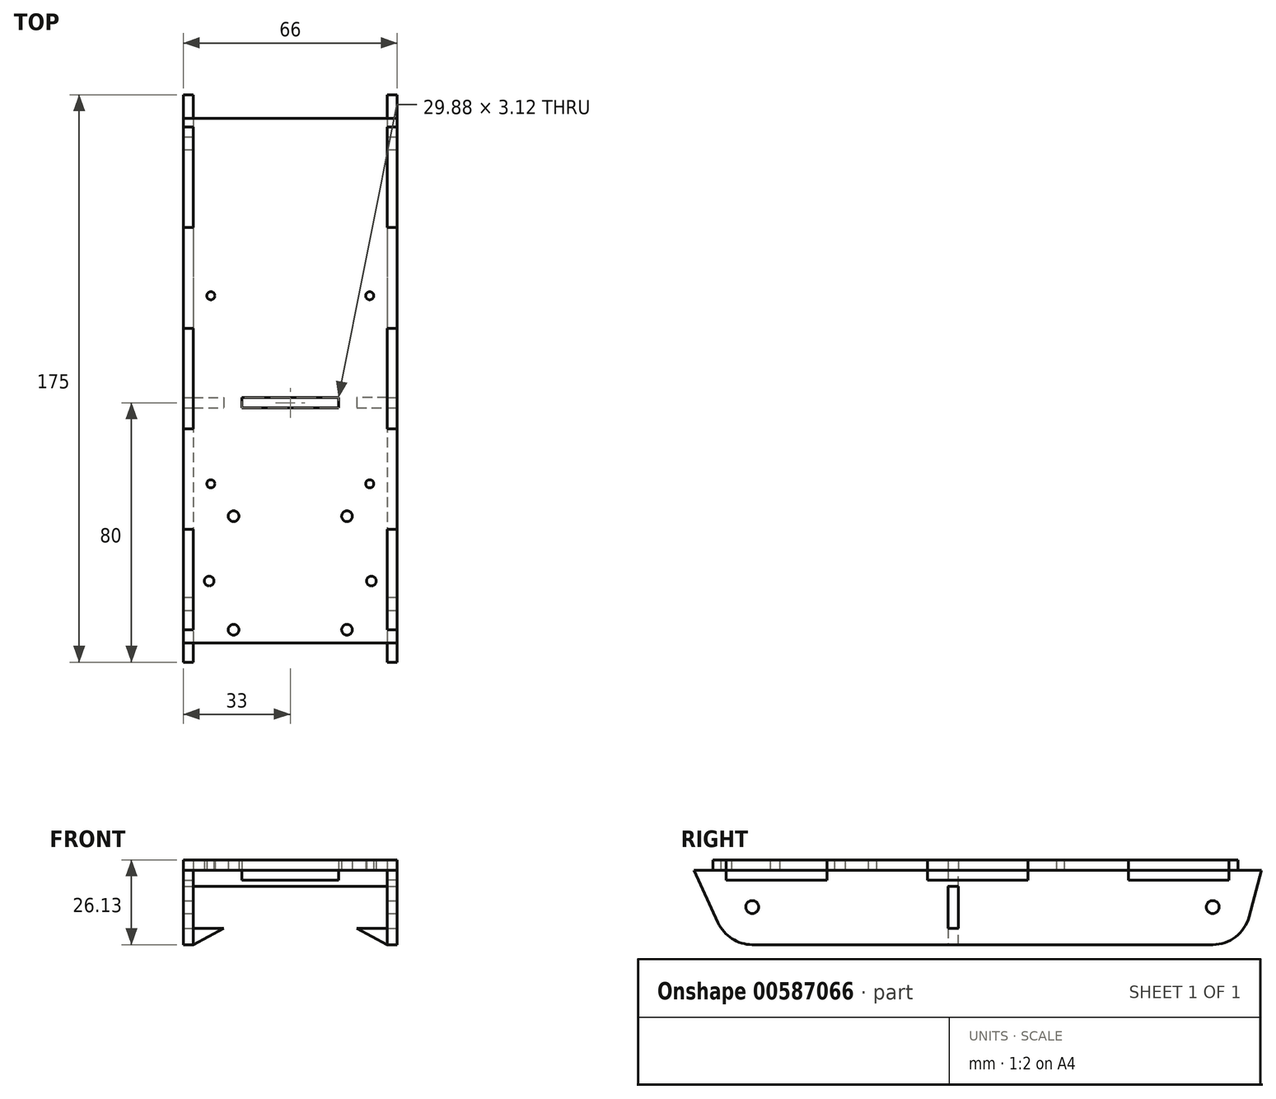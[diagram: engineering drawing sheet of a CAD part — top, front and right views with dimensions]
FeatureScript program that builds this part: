
annotation { "Feature Type Name" : "Feature", "Feature Type Description" : "" }
export const myFeature = defineFeature(function(context is Context, id is Id, definition is map)
    precondition{}
    {
        {
            var Q0;
            Q0=qCreatedBy(makeId("Top.planeOp"),FACE);
            var sketch = newSketch(context, id + "F0", { "sketchPlane" : qUnion([Q0])});
            skLineSegment(sketch, "E0.bottom", {"start": v(-33, 87.5) * mm, "end": v(33, 87.5) * mm});
            skLineSegment(sketch, "E0.top", {"start": v(-33, -87.5) * mm, "end": v(33, -87.5) * mm});
            skLineSegment(sketch, "E0.left", {"start": v(-33, 87.5) * mm, "end": v(-33, -87.5) * mm});
            skLineSegment(sketch, "E0.right", {"start": v(33, 87.5) * mm, "end": v(33, -87.5) * mm});
            skLineSegment(sketch, "E1", {"start": v(0, 87.5) * mm, "end": v(0, -87.5) * mm, "construction": true});
            skLineSegment(sketch, "E2", {"start": v(-33, 0) * mm, "end": v(33, 0) * mm, "construction": true});
            skCircle(sketch, "E3", {"center": v(-25, -62.5) * mm, "radius": 1.5 * mm});
            skCircle(sketch, "E4.MirrorC", {"center": v(25, -62.5) * mm, "radius": 1.5 * mm});
            skLineSegment(sketch, "E5", {"start": v(-50, -69.5) * mm, "end": v(50, -69.5) * mm, "construction": true});
            skLineSegment(sketch, "E6", {"start": v(-33.17, -7.5) * mm, "end": v(44.72, -7.5) * mm, "construction": true});
            skCircle(sketch, "E7", {"center": v(-24.5, 25.5) * mm, "radius": 1.25 * mm});
            skCircle(sketch, "E8", {"center": v(-24.5, -32.5) * mm, "radius": 1.25 * mm});
            skCircle(sketch, "E9.MirrorC", {"center": v(24.5, -32.5) * mm, "radius": 1.25 * mm});
            skCircle(sketch, "E10.MirrorC", {"center": v(24.5, 25.5) * mm, "radius": 1.25 * mm});
            skCircle(sketch, "E11", {"center": v(-17.5, -42.5) * mm, "radius": 1.65 * mm});
            skCircle(sketch, "E12", {"center": v(-17.5, -77.5) * mm, "radius": 1.65 * mm});
            skCircle(sketch, "E13.MirrorC", {"center": v(17.5, -77.5) * mm, "radius": 1.65 * mm});
            skCircle(sketch, "E14.MirrorC", {"center": v(17.5, -42.5) * mm, "radius": 1.65 * mm});
            skSolve(sketch);
        }
        {
            var Q0;
            Q0 = qSketchRegion(id + "F0", true);
            extrude(context, id + "F1", {"entities" : qUnion([Q0]), "depth" : 3.12 * mm, "offsetDistance" : 25 * mm});
        }
        {
            var Q0;
            Q0=qCreatedBy(makeId("Top.planeOp"),FACE);
            var sketch = newSketch(context, id + "F2", { "sketchPlane" : qUnion([Q0])});
            skLineSegment(sketch, "E15.bottom", {"start": v(-33, 87.5) * mm, "end": v(-29.88, 87.5) * mm});
            skLineSegment(sketch, "E15.top", {"start": v(-33, -87.5) * mm, "end": v(-29.87, -87.5) * mm});
            skLineSegment(sketch, "E15.left", {"start": v(-33, 87.5) * mm, "end": v(-33, -87.5) * mm});
            skLineSegment(sketch, "E15.right", {"start": v(-29.88, 87.5) * mm, "end": v(-29.87, -87.5) * mm});
            skLineSegment(sketch, "E16.MirrorCS", {"start": v(33, 87.5) * mm, "end": v(29.88, 87.5) * mm});
            skLineSegment(sketch, "E17.MirrorCS", {"start": v(33, -87.5) * mm, "end": v(29.87, -87.5) * mm});
            skLineSegment(sketch, "E18.MirrorCS", {"start": v(29.88, 87.5) * mm, "end": v(29.87, -87.5) * mm});
            skLineSegment(sketch, "E19.MirrorCS", {"start": v(33, 87.5) * mm, "end": v(33, -87.5) * mm});
            skSolve(sketch);
        }
        {
            var Q0;
            Q0 = qSketchRegion(id + "F2", true);
            extrude(context, id + "F3", {"entities" : qUnion([Q0]), "oppositeDirection" : true, "depth" : 23 * mm, "offsetDistance" : 25 * mm});
        }
        {
            var Q0;
            Q0=qCreatedBy(makeId("Right.planeOp"),FACE);
            var sketch = newSketch(context, id + "F4", { "sketchPlane" : qUnion([Q0])});
            skCircle(sketch, "E20", {"center": v(-69.5, -11.4) * mm, "radius": 2 * mm});
            skCircle(sketch, "E21", {"center": v(72.5, -11.4) * mm, "radius": 2 * mm});
            skLineSegment(sketch, "E22", {"start": v(80.27, 0) * mm, "end": v(80.27, 7.65) * mm});
            skLineSegment(sketch, "E23", {"start": v(80.27, 7.65) * mm, "end": v(-81.6, 7.65) * mm});
            skLineSegment(sketch, "E24", {"start": v(-81.6, 7.65) * mm, "end": v(-81.6, 0) * mm});
            skLineSegment(sketch, "E25", {"start": v(-87.5, 0) * mm, "end": v(-81.6, 0) * mm});
            skLineSegment(sketch, "E26", {"start": v(-87.5, 0) * mm, "end": v(-80.04, -16.24) * mm});
            skLineSegment(sketch, "E27", {"start": v(87.5, 0) * mm, "end": v(80.27, 0) * mm});
            skLineSegment(sketch, "E28", {"start": v(87.5, 0) * mm, "end": v(83.72, -14.36) * mm});
            skArc(sketch, "E29", {"start": v(83.72, -14.36) * mm, "mid": v(79.58, -20.59) * mm, "end": v(72.5, -23) * mm});
            skArc(sketch, "E30", {"start": v(-80.04, -16.24) * mm, "mid": v(-75.76, -21.17) * mm, "end": v(-69.5, -23) * mm});
            skLineSegment(sketch, "E31", {"start": v(72.5, -23) * mm, "end": v(-69.5, -23) * mm});
            skSolve(sketch);
        }
        {
            var Q0;
            Q0 = qSketchRegion(id + "F4", true);
            extrude(context, id + "F5", {"entities" : qUnion([Q0]), "operationType" : NewBodyOperationType.INTERSECT, "endBound" : BoundingType.THROUGH_ALL, "oppositeDirection" : true, "depth" : 25 * mm, "offsetDistance" : 25 * mm, "hasSecondDirection" : true, "secondDirectionBound" : BoundingType.THROUGH_ALL, "secondDirectionOppositeDirection" : false, "secondDirectionDepth" : 25 * mm});
        }
        {
            var Q0;
            Q0=qCreatedBy(makeId("Front.planeOp"),FACE);
            var sketch = newSketch(context, id + "F6", { "sketchPlane" : qUnion([Q0])});
            skLineSegment(sketch, "E32", {"start": v(0, 0) * mm, "end": v(-29.88, 0) * mm});
            skLineSegment(sketch, "E33", {"start": v(-29.88, 0) * mm, "end": v(-29.88, -23) * mm});
            skLineSegment(sketch, "E34", {"start": v(-29.88, -23) * mm, "end": v(-14.88, -15) * mm});
            skLineSegment(sketch, "E35", {"start": v(-14.88, -15) * mm, "end": v(0, -15) * mm});
            skLineSegment(sketch, "E36", {"start": v(0, 0) * mm, "end": v(0, -15) * mm, "construction": true});
            skLineSegment(sketch, "E37.MirrorCS", {"start": v(29.88, -23) * mm, "end": v(14.87, -15) * mm});
            skLineSegment(sketch, "E38.MirrorCS", {"start": v(14.88, -15) * mm, "end": v(0, -15) * mm});
            skLineSegment(sketch, "E39.MirrorCS", {"start": v(29.88, 0) * mm, "end": v(29.88, -23) * mm});
            skLineSegment(sketch, "E40.MirrorCS", {"start": v(0, 0) * mm, "end": v(29.88, 0) * mm});
            skSolve(sketch);
        }
        {
            var Q0;
            Q0 = qSketchRegion(id + "F6", true);
            var Q1;
            Q1=sQuery(id+"F0.wireOp",VERTEX,"E6.start");
            var Q2;
            Q2=sQuery(id+"F0.wireOp",VERTEX,"E6.end");
            extrude(context, id + "F7", {"entities" : qUnion([Q0]), "endBound" : BoundingType.UP_TO_VERTEX, "depth" : 3.12 * mm, "endBoundEntityVertex" : qUnion([Q1]), "hasOffset" : true, "offsetDistance" : (3.12 / 2) * mm, "offsetOppositeDirection" : true, "hasSecondDirection" : true, "secondDirectionBound" : BoundingType.UP_TO_VERTEX, "secondDirectionOppositeDirection" : false, "secondDirectionDepth" : (3.12 / 2) * mm, "secondDirectionBoundEntityVertex" : qUnion([Q2]), "hasSecondDirectionOffset" : true, "secondDirectionOffsetDistance" : (3.12 / 2) * mm});
        }
        {
            var Q0;
            Q0=qCreatedBy(makeId("Right.planeOp"),FACE);
            var sketch = newSketch(context, id + "F8", { "sketchPlane" : qUnion([Q0])});
            skLineSegment(sketch, "E41.bottom", {"start": v(-5.94, -18) * mm, "end": v(-9.06, -18) * mm});
            skLineSegment(sketch, "E41.top", {"start": v(-5.94, -5) * mm, "end": v(-9.06, -5) * mm});
            skLineSegment(sketch, "E41.left", {"start": v(-9.06, -18) * mm, "end": v(-9.06, -5) * mm});
            skLineSegment(sketch, "E41.right", {"start": v(-5.94, -18) * mm, "end": v(-5.94, -5) * mm});
            skLineSegment(sketch, "E42", {"start": v(-7.5, 0) * mm, "end": v(-7.5, -18) * mm, "construction": true});
            skSolve(sketch);
        }
        {
            var Q0;
            Q0 = qSketchRegion(id + "F8", true);
            var Q1;
            Q1=makeQuery(id+"F3.opExtrude","SWEPT_FACE",FACE,{"disambiguationData":[OSD([sQuery(id+"F2.wireOp",EDGE,"E19.MirrorCS")])]});
            var Q2;
            Q2=makeQuery(id+"F3.opExtrude","SWEPT_FACE",FACE,{"disambiguationData":[OSD([sQuery(id+"F2.wireOp",EDGE,"E15.left")])]});
            extrude(context, id + "F9", {"entities" : qUnion([Q0]), "operationType" : NewBodyOperationType.ADD, "endBound" : BoundingType.UP_TO_SURFACE, "depth" : 25 * mm, "endBoundEntityFace" : qUnion([Q1]), "offsetDistance" : 25 * mm, "hasSecondDirection" : true, "secondDirectionBound" : BoundingType.UP_TO_SURFACE, "secondDirectionOppositeDirection" : true, "secondDirectionDepth" : 25 * mm, "secondDirectionBoundEntityFace" : qUnion([Q2])});
        }
        {
            var Q0;
            Q0 = qSketchRegion(id + "F8", true);
            extrude(context, id + "F10", {"entities" : qUnion([Q0]), "operationType" : NewBodyOperationType.REMOVE, "endBound" : BoundingType.THROUGH_ALL, "oppositeDirection" : true, "depth" : 25 * mm, "offsetDistance" : 25 * mm, "hasSecondDirection" : true, "secondDirectionBound" : BoundingType.THROUGH_ALL, "secondDirectionOppositeDirection" : false, "secondDirectionDepth" : 25 * mm});
        }
        {
            var Q0;
            Q0=qCreatedBy(makeId("Top.planeOp"),FACE);
            var sketch = newSketch(context, id + "F11", { "sketchPlane" : qUnion([Q0])});
            skLineSegment(sketch, "E43.bottom", {"start": v(-33, 77.5) * mm, "end": v(-29.87, 77.5) * mm});
            skLineSegment(sketch, "E43.top", {"start": v(-33, 46.5) * mm, "end": v(-29.87, 46.5) * mm});
            skLineSegment(sketch, "E43.left", {"start": v(-33, 77.5) * mm, "end": v(-33, 46.5) * mm});
            skLineSegment(sketch, "E43.right", {"start": v(-29.88, 77.5) * mm, "end": v(-29.88, 46.5) * mm});
            skLineSegment(sketch, "E44.bottom", {"start": v(-33, 15.5) * mm, "end": v(-29.87, 15.5) * mm});
            skLineSegment(sketch, "E44.top", {"start": v(-33, -15.5) * mm, "end": v(-29.88, -15.5) * mm});
            skLineSegment(sketch, "E44.left", {"start": v(-33, 15.5) * mm, "end": v(-33, -15.5) * mm});
            skLineSegment(sketch, "E44.right", {"start": v(-29.88, 15.5) * mm, "end": v(-29.88, -15.5) * mm});
            skLineSegment(sketch, "E45.bottom", {"start": v(-14.94, -9.06) * mm, "end": v(0, -9.06) * mm});
            skLineSegment(sketch, "E45.top", {"start": v(-14.94, -5.94) * mm, "end": v(0, -5.94) * mm});
            skLineSegment(sketch, "E45.left", {"start": v(-14.94, -9.06) * mm, "end": v(-14.94, -5.94) * mm});
            skLineSegment(sketch, "E46.bottom", {"start": v(-33, -46.5) * mm, "end": v(-29.87, -46.5) * mm});
            skLineSegment(sketch, "E46.top", {"start": v(-33, -77.5) * mm, "end": v(-29.88, -77.5) * mm});
            skLineSegment(sketch, "E46.left", {"start": v(-33, -46.5) * mm, "end": v(-33, -77.5) * mm});
            skLineSegment(sketch, "E46.right", {"start": v(-29.88, -46.5) * mm, "end": v(-29.88, -77.5) * mm});
            skLineSegment(sketch, "E47", {"start": v(-33, 46.5) * mm, "end": v(-33, 15.5) * mm, "construction": true});
            skLineSegment(sketch, "E48", {"start": v(-33, -15.5) * mm, "end": v(-33, -46.5) * mm, "construction": true});
            skLineSegment(sketch, "E49.MirrorCS", {"start": v(14.94, -9.06) * mm, "end": v(14.94, -5.94) * mm});
            skLineSegment(sketch, "E50.MirrorCS", {"start": v(14.94, -9.06) * mm, "end": v(0, -9.06) * mm});
            skLineSegment(sketch, "E51.MirrorCS", {"start": v(14.94, -5.94) * mm, "end": v(0, -5.94) * mm});
            skLineSegment(sketch, "E52.MirrorCS", {"start": v(33, -77.5) * mm, "end": v(29.88, -77.5) * mm});
            skLineSegment(sketch, "E53.MirrorCS", {"start": v(33, -46.5) * mm, "end": v(29.88, -46.5) * mm});
            skLineSegment(sketch, "E54.MirrorCS", {"start": v(33, -15.5) * mm, "end": v(29.88, -15.5) * mm});
            skLineSegment(sketch, "E55.MirrorCS", {"start": v(33, 15.5) * mm, "end": v(29.87, 15.5) * mm});
            skLineSegment(sketch, "E56.MirrorCS", {"start": v(33, 46.5) * mm, "end": v(29.87, 46.5) * mm});
            skLineSegment(sketch, "E57.MirrorCS", {"start": v(33, 77.5) * mm, "end": v(29.87, 77.5) * mm});
            skLineSegment(sketch, "E58.MirrorCS", {"start": v(29.88, 15.5) * mm, "end": v(29.88, -15.5) * mm});
            skLineSegment(sketch, "E59.MirrorCS", {"start": v(33, 15.5) * mm, "end": v(33, -15.5) * mm});
            skLineSegment(sketch, "E60.MirrorCS", {"start": v(33, -15.5) * mm, "end": v(33, -46.5) * mm, "construction": true});
            skLineSegment(sketch, "E61.MirrorCS", {"start": v(29.88, 77.5) * mm, "end": v(29.88, 46.5) * mm});
            skLineSegment(sketch, "E62.MirrorCS", {"start": v(33, 77.5) * mm, "end": v(33, 46.5) * mm});
            skLineSegment(sketch, "E63.MirrorCS", {"start": v(33, 46.5) * mm, "end": v(33, 15.5) * mm, "construction": true});
            skLineSegment(sketch, "E64.MirrorCS", {"start": v(29.88, -46.5) * mm, "end": v(29.88, -77.5) * mm});
            skLineSegment(sketch, "E65.MirrorCS", {"start": v(33, -46.5) * mm, "end": v(33, -77.5) * mm});
            skLineSegment(sketch, "E66", {"start": v(-14.94, -7.5) * mm, "end": v(-29.87, -7.5) * mm, "construction": true});
            skSolve(sketch);
        }
        {
            var Q0;
            Q0 = qSketchRegion(id + "F11", true);
            extrude(context, id + "F12", {"entities" : qUnion([Q0]), "operationType" : NewBodyOperationType.REMOVE, "depth" : 25 * mm, "offsetDistance" : 25 * mm});
        }
        {
            var Q0;
            Q0 = qSketchRegion(id + "F11", true);
            extrude(context, id + "F13", {"entities" : qUnion([Q0]), "depth" : 3.12 * mm, "offsetDistance" : 25 * mm, "hasSecondDirection" : true, "secondDirectionOppositeDirection" : true, "secondDirectionDepth" : 3.12 * mm});
        }
    });
